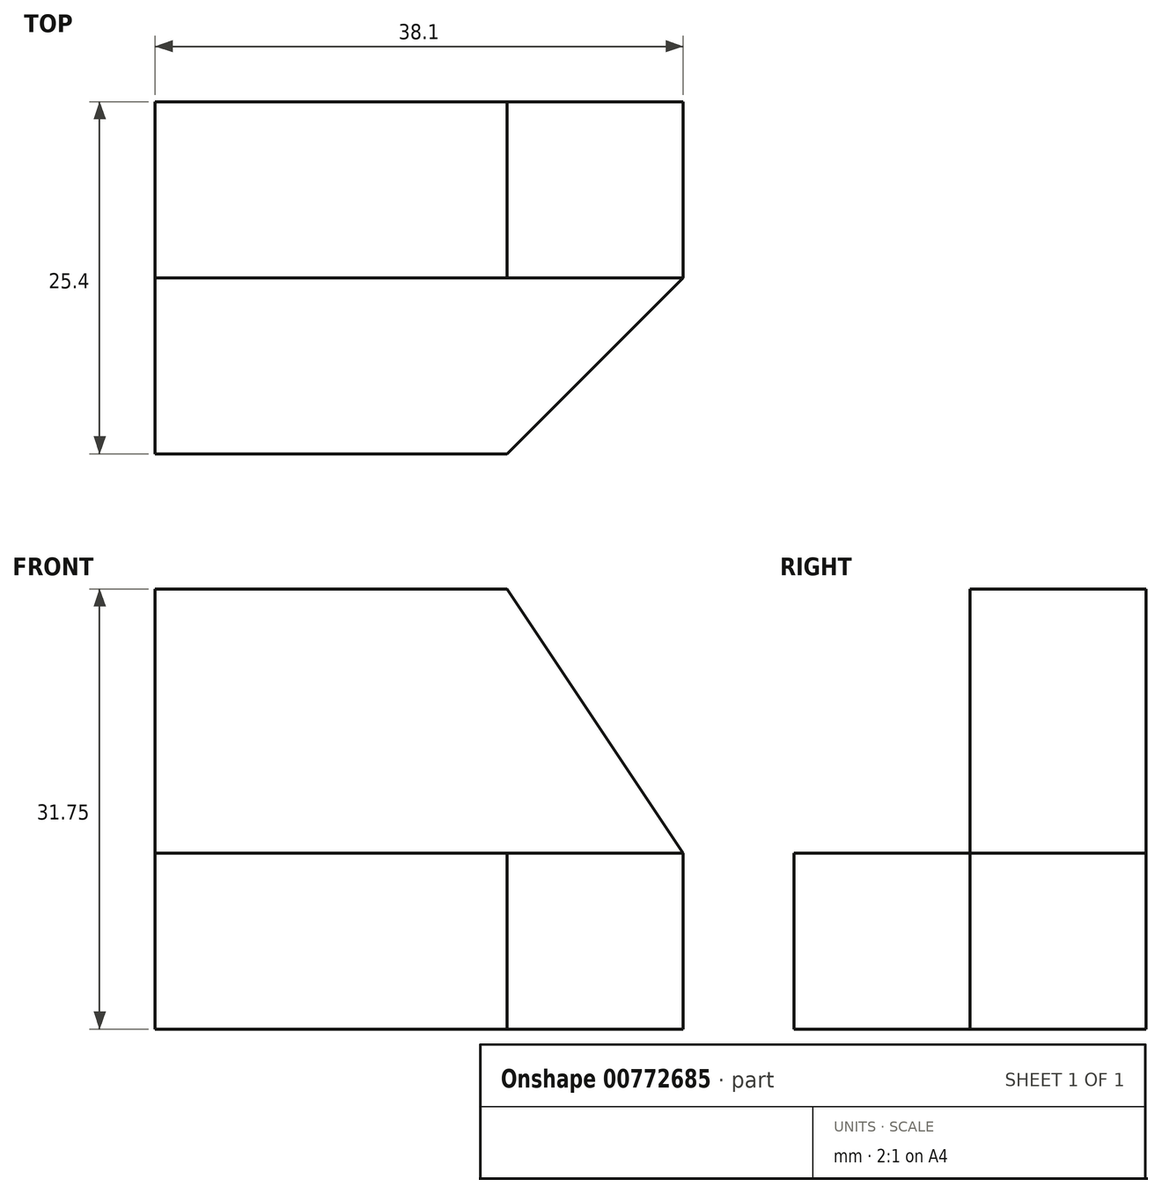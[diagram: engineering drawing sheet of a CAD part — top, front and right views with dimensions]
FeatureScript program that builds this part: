
annotation { "Feature Type Name" : "Feature", "Feature Type Description" : "" }
export const myFeature = defineFeature(function(context is Context, id is Id, definition is map)
    precondition{}
    {
        {
            var Q0;
            Q0=qCreatedBy(makeId("Front.planeOp"),FACE);
            var sketch = newSketch(context, id + "F0", { "sketchPlane" : qUnion([Q0])});
            skLineSegment(sketch, "E0", {"start": v(0, 0) * mm, "end": v(38.1, 0) * mm});
            skLineSegment(sketch, "E1", {"start": v(0, 0) * mm, "end": v(0, 31.75) * mm});
            skLineSegment(sketch, "E2", {"start": v(0, 31.75) * mm, "end": v(38.1, 31.75) * mm});
            skLineSegment(sketch, "E3", {"start": v(38.1, 31.75) * mm, "end": v(38.1, 0) * mm});
            skSolve(sketch);
        }
        {
            var Q0;
            Q0=makeQuery(id+"F0.imprint","IMPRINT",FACE,{"disambiguationData":[TD([[makeQuery(id+"F0.imprint","IMPRINT",EDGE,{"derivedFrom":sQuery(id+"F0.wireOp",EDGE,"E0")}),1.0]])]});
            extrude(context, id + "F1", {"entities" : qUnion([Q0]), "depth" : 25.4 * mm, "offsetDistance" : 25.4 * mm});
        }
        {
            var Q0;
            Q0=makeQuery(id+"F1.opExtrude","SWEPT_FACE",FACE,{"disambiguationData":[OSD([sQuery(id+"F0.wireOp",EDGE,"E3")])]});
            var sketch = newSketch(context, id + "F2", { "sketchPlane" : qUnion([Q0])});
            skLineSegment(sketch, "E4", {"start": v(-25.4, 0) * mm, "end": v(-25.4, 12.7) * mm});
            skLineSegment(sketch, "E5", {"start": v(-25.4, 12.7) * mm, "end": v(-12.7, 12.7) * mm});
            skLineSegment(sketch, "E6", {"start": v(-12.7, 12.7) * mm, "end": v(-12.7, 31.75) * mm});
            skLineSegment(sketch, "E7", {"start": v(-12.7, 31.75) * mm, "end": v(0, 31.75) * mm});
            skSolve(sketch);
        }
        {
            var Q0;
            {var subQ0=sQuery(id+"F2.wireOp",EDGE,"E5");Q0=makeQuery(id+"F2.imprint","IMPRINT",FACE,{"disambiguationData":[TD([[makeQuery(id+"F2.imprint","IMPRINT",EDGE,{"derivedFrom":subQ0}),1.0]])]});}
            extrude(context, id + "F3", {"entities" : qUnion([Q0]), "operationType" : NewBodyOperationType.REMOVE, "oppositeDirection" : true, "depth" : 38.1 * mm, "offsetDistance" : 25.4 * mm});
        }
        {
            var Q0;
            Q0=makeQuery(id+"F3.boolean.opBoolean","COPY",FACE,{"derivedFrom":makeQuery(id+"F3.opExtrude","SWEPT_FACE",FACE,{"disambiguationData":[OSD([sQuery(id+"F2.wireOp",EDGE,"E6")])]})});
            var sketch = newSketch(context, id + "F4", { "sketchPlane" : qUnion([Q0])});
            skLineSegment(sketch, "E8", {"start": v(38.1, 31.75) * mm, "end": v(25.4, 31.75) * mm});
            skLineSegment(sketch, "E9", {"start": v(25.4, 31.75) * mm, "end": v(38.1, 12.7) * mm});
            skSolve(sketch);
        }
        {
            var Q0;
            Q0=makeQuery(id+"F4.imprint","IMPRINT",FACE,{"disambiguationData":[TD([[makeQuery(id+"F4.imprint","IMPRINT",EDGE,{"derivedFrom":sQuery(id+"F4.wireOp",EDGE,"E8")}),-1.0]])]});
            extrude(context, id + "F5", {"entities" : qUnion([Q0]), "operationType" : NewBodyOperationType.REMOVE, "oppositeDirection" : true, "depth" : 25.4 * mm, "offsetDistance" : 25.4 * mm});
        }
        {
            var Q0;
            Q0=makeQuery(id+"F3.boolean.opBoolean","COPY",FACE,{"derivedFrom":makeQuery(id+"F3.opExtrude","SWEPT_FACE",FACE,{"disambiguationData":[OSD([sQuery(id+"F2.wireOp",EDGE,"E5")])]})});
            var sketch = newSketch(context, id + "F6", { "sketchPlane" : qUnion([Q0])});
            skLineSegment(sketch, "E10", {"start": v(38.1, -25.4) * mm, "end": v(25.4, -25.4) * mm});
            skLineSegment(sketch, "E11", {"start": v(25.4, -25.4) * mm, "end": v(38.1, -12.7) * mm});
            skSolve(sketch);
        }
        {
            var Q0;
            Q0=makeQuery(id+"F6.imprint","IMPRINT",FACE,{"disambiguationData":[TD([[makeQuery(id+"F6.imprint","IMPRINT",EDGE,{"derivedFrom":sQuery(id+"F6.wireOp",EDGE,"E10")}),1.0]])]});
            extrude(context, id + "F7", {"entities" : qUnion([Q0]), "operationType" : NewBodyOperationType.REMOVE, "oppositeDirection" : true, "depth" : 25.4 * mm, "offsetDistance" : 25.4 * mm});
        }
    });
